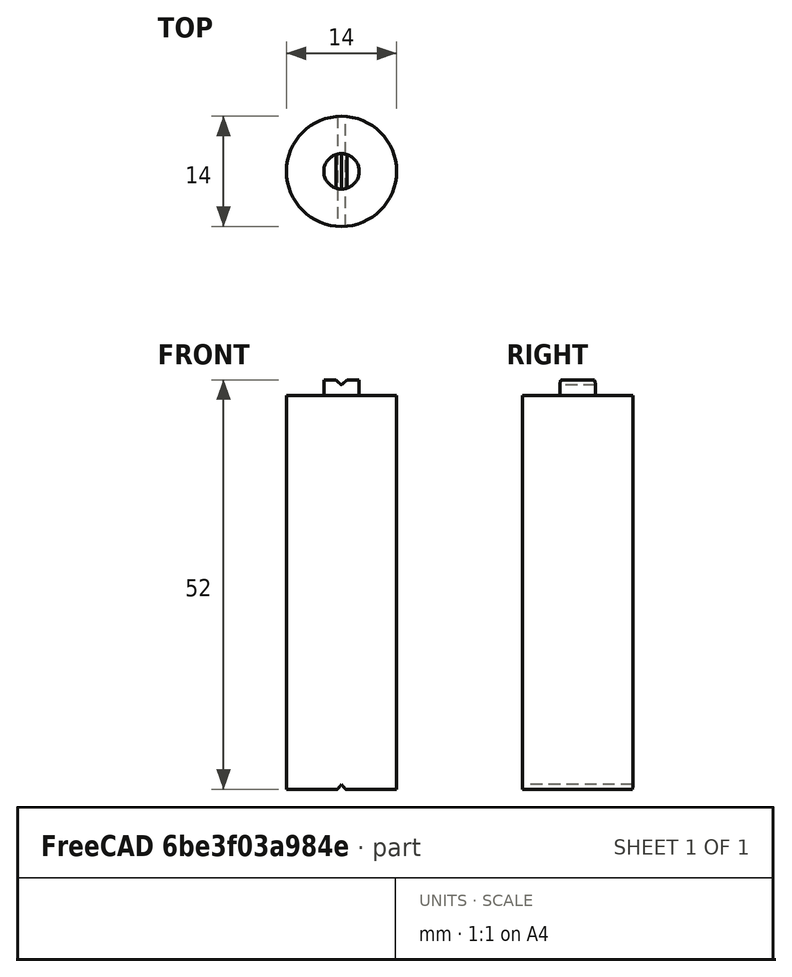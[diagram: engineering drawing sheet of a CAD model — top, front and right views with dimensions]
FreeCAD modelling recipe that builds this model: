
FCSTD DOCUMENT  (FreeCAD 0.16R)
Label: 14500notch
License: All rights reserved
LicenseURL: http://en.wikipedia.org/wiki/All_rights_reserved
objects: Sketcher::SketchObject×3, PartDesign::Pad×3, Part::MultiFuse×1, Part::Cut×1, Mesh::Feature×1
note: 11 computed .brp shape members not serialized (recipe doc carries the construction recipe); baked Part::Feature solids carry a one-line shape summary decoded from their .brp

FEATURE [Sketcher::SketchObject] Sketch
  sketch-geometry (1):
    g0: Circle CenterX=0 CenterY=0 CenterZ=0 NormalX=0 NormalY=0 NormalZ=1 Radius=7
  constraints (2):
    c: Coincident(g0,g-1)
    c: Radius(g0) = 7
FEATURE [PartDesign::Pad] Pad
  Length = 50
  Length2 = 100
  Sketch = -> Sketch
  Type = 0
FEATURE [Sketcher::SketchObject] Sketch001
  Placement = pos=(0,0,50) rot=(0,0,1;0rad)
  Support = -> Pad [Face3]
  sketch-geometry (1):
    g0: Circle CenterX=0 CenterY=0 CenterZ=0 NormalX=0 NormalY=0 NormalZ=1 Radius=2.25
  constraints (2):
    c: Coincident(g0,g-1)
    c: Radius(g0) = 2.25
FEATURE [PartDesign::Pad] Pad001
  Length = 2
  Length2 = 100
  Sketch = -> Sketch001
  Type = 0
FEATURE [Sketcher::SketchObject] Sketch002
  Placement = pos=(0,0,0) rot=(-1,0,0;4.71239rad)
  sketch-geometry (6):
    g0: LineSegment StartX=0 StartY=0.620628 StartZ=0 EndX=3.8275 EndY=-4 EndZ=0
    g1: LineSegment StartX=3.8275 StartY=-4 StartZ=0 EndX=-3.8275 EndY=-4 EndZ=0
    g2: LineSegment StartX=-3.8275 StartY=-4 StartZ=0 EndX=0 EndY=0.620628 EndZ=0
    g3: LineSegment StartX=-4.5 StartY=55.3327 StartZ=0 EndX=0 EndY=51.3641 EndZ=0
    g4: LineSegment StartX=0 StartY=51.3641 StartZ=0 EndX=4.5 EndY=55.3327 EndZ=0
    g5: LineSegment StartX=4.5 StartY=55.3327 StartZ=0 EndX=-4.5 EndY=55.3327 EndZ=0
  constraints (18):
    c: Coincident(g0,g1)
    c: Horizontal(g1)
    c: Coincident(g1,g2)
    c: Coincident(g2,g0)
    c: PointOnObject(g0,g-2)
    c: Symmetric(g1,g0,g-2)
    c: DistanceY(g0) = -4
    c: Distance(g0) = 6
    c: Coincident(g3,g4)
    c: Coincident(g4,g5)
    c: Coincident(g3,g5)
    c: Horizontal(g5)
    c: Symmetric(g4,g3,g-2)
    c: Distance(g4) = 6
    c: PointOnObject(g3,g-2)
    c: Distance(g5) = 9
    c: DistanceY(g4) = 55.3327
    c: Distance(g1) = 7.65501
FEATURE [PartDesign::Pad] Pad002
  Length = 20
  Length2 = 100
  Midplane = true
  Placement = pos=(0,0,0) rot=(-1,0,0;4.71239rad)
  Sketch = -> Sketch002
  Type = 0
FEATURE [Part::MultiFuse] Fusion
  Shapes = -> [Pad001,Pad]
FEATURE [Part::Cut] Cut
  Base = -> Fusion
  Tool = -> Pad002
FEATURE [Mesh::Feature] Mesh  label="Cut (Meshed)"
